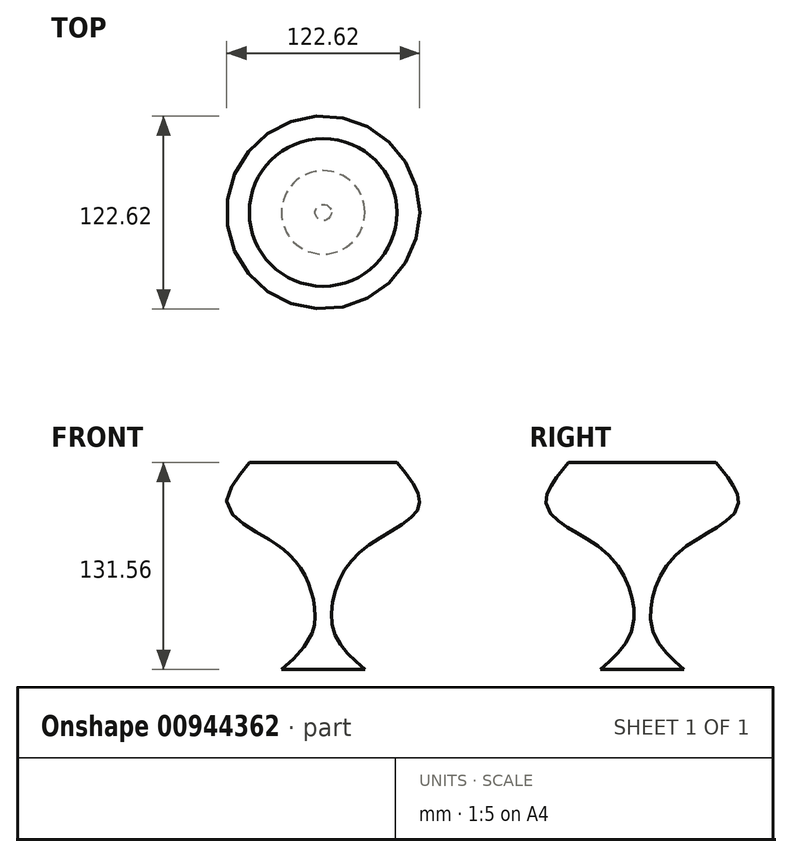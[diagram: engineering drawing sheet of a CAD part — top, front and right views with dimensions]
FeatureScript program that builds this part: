
annotation { "Feature Type Name" : "Feature", "Feature Type Description" : "" }
export const myFeature = defineFeature(function(context is Context, id is Id, definition is map)
    precondition{}
    {
        {
            var Q0;
            Q0=qCreatedBy(makeId("Top.planeOp"),FACE);
            var sketch = newSketch(context, id + "F0", { "sketchPlane" : qUnion([Q0])});
            skCircle(sketch, "E0", {"center": v(0, 0) * mm, "radius": 8.23 * mm});
            skSolve(sketch);
        }
        {
            var Q0;
            Q0=qCreatedBy(makeId("Top.planeOp"),FACE);
            cPlane(context, id + "F1", {"entities" : qUnion([Q0]), "cplaneType" : CPlaneType.OFFSET, "offset" : 80 * mm, "width" : 152.4 * mm, "height" : 152.4 * mm});
        }
        {
            var Q0;
            Q0=qCreatedBy(id+"F1.planeOp",FACE);
            var sketch = newSketch(context, id + "F2", { "sketchPlane" : qUnion([Q0])});
            skCircle(sketch, "E1", {"center": v(0, 0) * mm, "radius": 46.9 * mm});
            skSolve(sketch);
        }
        {
            var Q0;
            Q0=qCreatedBy(makeId("Top.planeOp"),FACE);
            cPlane(context, id + "F3", {"entities" : qUnion([Q0]), "cplaneType" : CPlaneType.OFFSET, "offset" : 54.1 * mm, "width" : 152.4 * mm, "height" : 152.4 * mm});
        }
        {
            var Q0;
            Q0=qCreatedBy(makeId("Top.planeOp"),FACE);
            cPlane(context, id + "F4", {"entities" : qUnion([Q0]), "cplaneType" : CPlaneType.OFFSET, "offset" : 25.4 * mm, "width" : 152.4 * mm, "height" : 152.4 * mm});
        }
        {
            var Q0;
            Q0=qCreatedBy(id+"F4.planeOp",FACE);
            var sketch = newSketch(context, id + "F5", { "sketchPlane" : qUnion([Q0])});
            skCircle(sketch, "E2", {"center": v(0, 0) * mm, "radius": 26.1 * mm});
            skSolve(sketch);
        }
        {
            var Q0;
            Q0=qCreatedBy(makeId("Top.planeOp"),FACE);
            cPlane(context, id + "F6", {"entities" : qUnion([Q0]), "cplaneType" : CPlaneType.OFFSET, "offset" : 26.42 * mm, "oppositeDirection" : true, "width" : 152.4 * mm, "height" : 152.4 * mm});
        }
        {
            var Q0;
            Q0=qCreatedBy(id+"F6.planeOp",FACE);
            cPlane(context, id + "F7", {"entities" : qUnion([Q0]), "cplaneType" : CPlaneType.OFFSET, "offset" : 25.15 * mm, "oppositeDirection" : true, "width" : 152.4 * mm, "height" : 152.4 * mm});
        }
        {
            var Q0;
            Q0=qCreatedBy(id+"F6.planeOp",FACE);
            var sketch = newSketch(context, id + "F8", { "sketchPlane" : qUnion([Q0])});
            skCircle(sketch, "E3", {"center": v(0, 0) * mm, "radius": 6.4 * mm});
            skSolve(sketch);
        }
        {
            var Q0;
            Q0=qCreatedBy(id+"F7.planeOp",FACE);
            var sketch = newSketch(context, id + "F9", { "sketchPlane" : qUnion([Q0])});
            skCircle(sketch, "E4", {"center": v(0, 0) * mm, "radius": 26.48 * mm});
            skSolve(sketch);
        }
        {
            var Q0;
            Q0=qCreatedBy(id+"F3.planeOp",FACE);
            var sketch = newSketch(context, id + "F10", { "sketchPlane" : qUnion([Q0])});
            skCircle(sketch, "E5", {"center": v(0, 0) * mm, "radius": 61.26 * mm});
            skSolve(sketch);
        }
        {
            var Q0;
            Q0=makeQuery(id+"F2.imprint","IMPRINT",FACE,{"disambiguationData":[TD([[makeQuery(id+"F2.imprint","IMPRINT",EDGE,{"derivedFrom":sQuery(id+"F2.wireOp",EDGE,"E1")}),1.0]])]});
            var Q1;
            Q1=makeQuery(id+"F10.imprint","IMPRINT",FACE,{"disambiguationData":[TD([[makeQuery(id+"F10.imprint","IMPRINT",EDGE,{"derivedFrom":sQuery(id+"F10.wireOp",EDGE,"E5")}),1.0]])]});
            var Q2;
            Q2=makeQuery(id+"F5.imprint","IMPRINT",FACE,{"disambiguationData":[TD([[makeQuery(id+"F5.imprint","IMPRINT",EDGE,{"derivedFrom":sQuery(id+"F5.wireOp",EDGE,"E2")}),1.0]])]});
            var Q3;
            Q3=makeQuery(id+"F0.imprint","IMPRINT",FACE,{"disambiguationData":[TD([[makeQuery(id+"F0.imprint","IMPRINT",EDGE,{"derivedFrom":sQuery(id+"F0.wireOp",EDGE,"E0")}),1.0]])]});
            var Q4;
            Q4=makeQuery(id+"F8.imprint","IMPRINT",FACE,{"disambiguationData":[TD([[makeQuery(id+"F8.imprint","IMPRINT",EDGE,{"derivedFrom":sQuery(id+"F8.wireOp",EDGE,"E3")}),1.0]])]});
            var Q5;
            Q5=makeQuery(id+"F9.imprint","IMPRINT",FACE,{"disambiguationData":[TD([[makeQuery(id+"F9.imprint","IMPRINT",EDGE,{"derivedFrom":sQuery(id+"F9.wireOp",EDGE,"E4")}),1.0]])]});
            loft(context, id + "F11", {"sheetProfilesArray" : [{ "sheetProfileEntities" : qUnion([Q0]) }, { "sheetProfileEntities" : qUnion([Q1]) }, { "sheetProfileEntities" : qUnion([Q2]) }, { "sheetProfileEntities" : qUnion([Q3]) }, { "sheetProfileEntities" : qUnion([Q4]) }, { "sheetProfileEntities" : qUnion([Q5]) }]});
        }
    });
